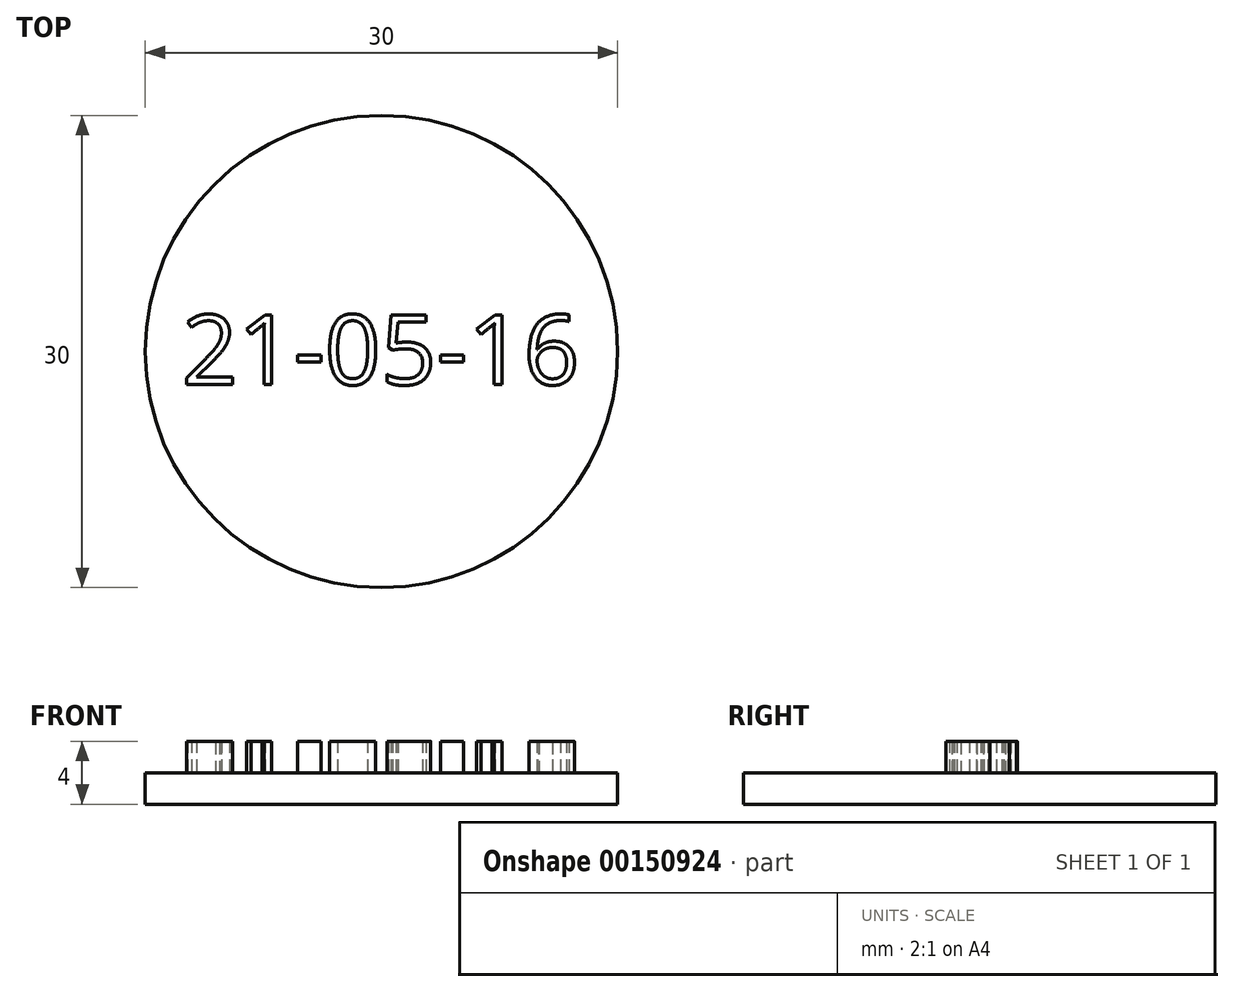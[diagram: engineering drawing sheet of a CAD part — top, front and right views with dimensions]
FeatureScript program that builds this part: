
annotation { "Feature Type Name" : "Feature", "Feature Type Description" : "" }
export const myFeature = defineFeature(function(context is Context, id is Id, definition is map)
    precondition{}
    {
        {
            var Q0;
            Q0=qCreatedBy(makeId("Top.planeOp"),FACE);
            var sketch = newSketch(context, id + "F0", { "sketchPlane" : qUnion([Q0])});
            skCircle(sketch, "E0", {"center": v(0, 0) * mm, "radius": 15 * mm});
            skSolve(sketch);
        }
        {
            var Q0;
            Q0=makeQuery(id+"F0.imprint","IMPRINT",FACE,{"disambiguationData":[TD([[makeQuery(id+"F0.imprint","IMPRINT",EDGE,{"derivedFrom":sQuery(id+"F0.wireOp",EDGE,"E0")}),1.0]])]});
            extrude(context, id + "F1", {"entities" : qUnion([Q0]), "depth" : 2 * mm});
        }
        {
            var Q0;
            Q0=makeQuery(id+"F1.opExtrude","CAP_FACE",FACE,{"disambiguationData":[OSD([sQuery(id+"F0.wireOp",EDGE,"E0")])],"isStart":false});
            var sketch = newSketch(context, id + "F2", { "sketchPlane" : qUnion([Q0])});
            skText(sketch, "E1", { "text": "21-05-16\n", "fontName": "OpenSans-Regular.ttf"});
            const initialGuessF2  = {"E1": [-0.01267, -0.0021, 1, 0, 0.00446]};
            skSetInitialGuess(sketch, initialGuessF2);
            skSolve(sketch);
        }
        {
            var Q0;
            Q0 = qSketchRegion(id + "F2", true);
            extrude(context, id + "F3", {"entities" : qUnion([Q0]), "operationType" : NewBodyOperationType.ADD, "depth" : 2 * mm});
        }
    });
